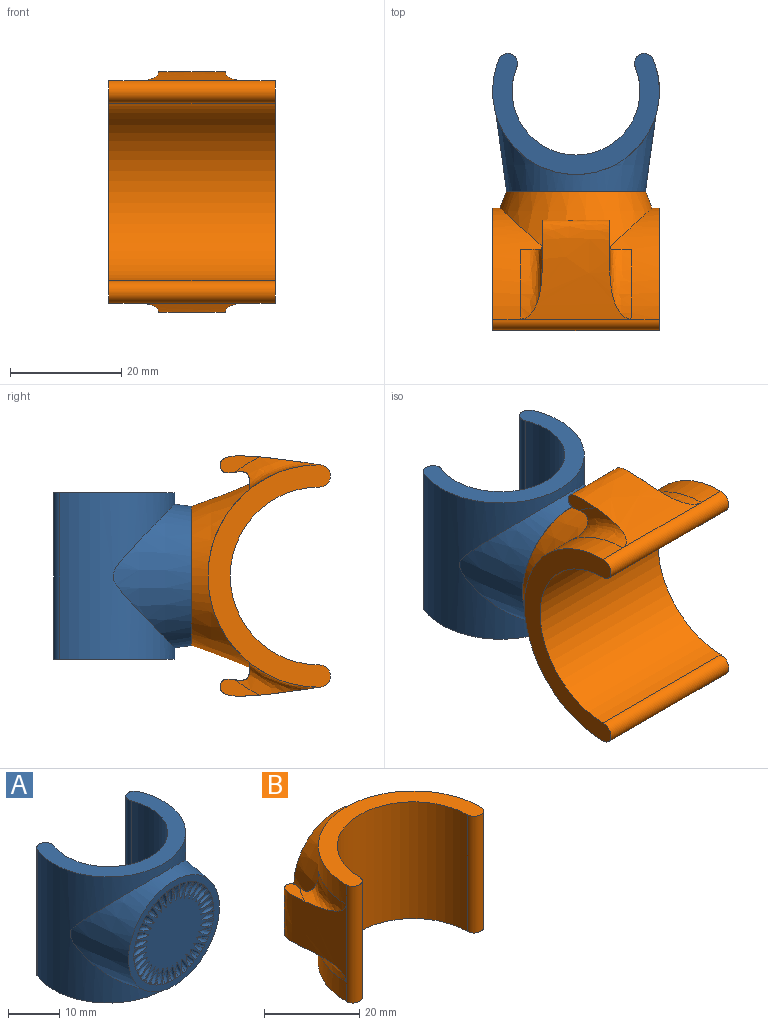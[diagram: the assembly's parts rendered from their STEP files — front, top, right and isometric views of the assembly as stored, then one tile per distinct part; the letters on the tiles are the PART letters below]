
ASSEMBLY  parts=2 mates=1
PART A: 190 faces, bbox 30.1x24.8x30 mm
  f0: cylinder r=15mm len=30mm, axis (0,0,-1), area 1052.1mm2, adj f2,f3,f4,f5,f6,f80,f81,f82
  f1: cylinder r=11.5mm len=30mm, axis (0,0,-1), area 1351.6mm2, adj f2,f3,f4,f5
  f2: cylinder r=1.75mm len=30mm, axis (0,0,-1), area 164.9mm2, adj f0,f1,f4,f5
  f3: cylinder r=1.75mm len=30mm, axis (0,0,-1), area 164.9mm2, adj f0,f1,f4,f5
  f4: plane 30x21.76mm, normal (0,0,1), area 191.3mm2, adj f0,f1,f2,f3
  f5: plane 30x21.76mm, normal (0,0,-1), area 191.3mm2, adj f0,f1,f2,f3
  f6: cone r=12.5mm half-angle=8deg, axis (0,1,0), area 605.5mm2, adj f0,f7
  f7: plane 25.03x25.03mm, normal (0,-1,0), area 357.3mm2, adj f6,f8,f9,f10,f11,f12,f13,f14
  f8: bspline ~3.54x0.78mm, area 2.7mm2, adj f7,f9
  f9: bspline ~3.52x0.92mm, area 2.7mm2, adj f7,f8
  f10: bspline ~3.51x1.07mm, area 2.7mm2, adj f7,f11
  f11: bspline ~3.55x0.84mm, area 2.7mm2, adj f7,f10
  f12: bspline ~3.43x1.64mm, area 2.7mm2, adj f7,f13
  f13: bspline ~3.53x1.2mm, area 2.7mm2, adj f7,f12
  f14: bspline ~3.24x2.17mm, area 2.7mm2, adj f7,f15
  f15: bspline ~3.42x1.75mm, area 2.7mm2, adj f7,f14
  f16: bspline ~2.95x2.62mm, area 2.7mm2, adj f7,f17
  f17: bspline ~3.21x2.26mm, area 2.7mm2, adj f7,f16
  f18: bspline ~3x2.58mm, area 2.7mm2, adj f7,f19
  f19: bspline ~2.9x2.69mm, area 2.7mm2, adj f7,f18
  f20: bspline ~3.28x2.12mm, area 2.7mm2, adj f7,f21
  f21: bspline ~3.04x2.5mm, area 2.7mm2, adj f7,f20
  f22: bspline ~3.46x1.6mm, area 2.7mm2, adj f7,f23
  f23: bspline ~3.3x2.03mm, area 2.7mm2, adj f7,f22
  f24: bspline ~3.54x1.05mm, area 2.7mm2, adj f7,f25
  f25: bspline ~3.46x1.49mm, area 2.7mm2, adj f7,f24
  f26: bspline ~3.54x0.78mm, area 2.7mm2, adj f7,f27
  f27: bspline ~3.52x0.92mm, area 2.7mm2, adj f7,f26
  f28: bspline ~3.51x1.07mm, area 2.7mm2, adj f7,f29
  f29: bspline ~3.55x0.84mm, area 2.7mm2, adj f7,f28
  f30: bspline ~3.43x1.64mm, area 2.7mm2, adj f7,f31
  f31: bspline ~3.53x1.2mm, area 2.7mm2, adj f7,f30
  f32: bspline ~3.24x2.17mm, area 2.7mm2, adj f7,f33
  f33: bspline ~3.42x1.75mm, area 2.7mm2, adj f7,f32
  f34: bspline ~2.95x2.62mm, area 2.7mm2, adj f7,f35
  f35: bspline ~3.21x2.26mm, area 2.7mm2, adj f7,f34
  f36: bspline ~3x2.58mm, area 2.7mm2, adj f7,f37
  f37: bspline ~2.9x2.69mm, area 2.7mm2, adj f7,f36
  f38: bspline ~3.28x2.12mm, area 2.7mm2, adj f7,f39
  f39: bspline ~3.04x2.5mm, area 2.7mm2, adj f7,f38
  f40: bspline ~3.46x1.6mm, area 2.7mm2, adj f7,f41
  f41: bspline ~3.3x2.03mm, area 2.7mm2, adj f7,f40
  f42: bspline ~3.54x1.05mm, area 2.7mm2, adj f7,f43
  f43: bspline ~3.46x1.49mm, area 2.7mm2, adj f7,f42
  f44: bspline ~3.54x0.78mm, area 2.7mm2, adj f7,f45
  f45: bspline ~3.52x0.92mm, area 2.7mm2, adj f7,f44
  f46: bspline ~3.51x1.07mm, area 2.7mm2, adj f7,f47
  f47: bspline ~3.55x0.84mm, area 2.7mm2, adj f7,f46
  f48: bspline ~3.43x1.64mm, area 2.7mm2, adj f7,f49
  f49: bspline ~3.53x1.2mm, area 2.7mm2, adj f7,f48
  f50: bspline ~3.24x2.17mm, area 2.7mm2, adj f7,f51
  f51: bspline ~3.42x1.75mm, area 2.7mm2, adj f7,f50
  f52: bspline ~2.95x2.62mm, area 2.7mm2, adj f7,f53
  f53: bspline ~3.21x2.26mm, area 2.7mm2, adj f7,f52
  f54: bspline ~3x2.58mm, area 2.7mm2, adj f7,f55
  f55: bspline ~2.9x2.69mm, area 2.7mm2, adj f7,f54
  f56: bspline ~3.28x2.12mm, area 2.7mm2, adj f7,f57
  f57: bspline ~3.04x2.5mm, area 2.7mm2, adj f7,f56
  f58: bspline ~3.46x1.6mm, area 2.7mm2, adj f7,f59
  f59: bspline ~3.3x2.03mm, area 2.7mm2, adj f7,f58
  f60: bspline ~3.54x1.05mm, area 2.7mm2, adj f7,f61
  f61: bspline ~3.46x1.49mm, area 2.7mm2, adj f7,f60
  f62: bspline ~3.54x0.78mm, area 2.7mm2, adj f7,f63
  f63: bspline ~3.52x0.92mm, area 2.7mm2, adj f7,f62
  f64: bspline ~3.51x1.07mm, area 2.7mm2, adj f7,f65
  f65: bspline ~3.55x0.84mm, area 2.7mm2, adj f7,f64
  f66: bspline ~3.43x1.64mm, area 2.7mm2, adj f7,f67
  f67: bspline ~3.53x1.2mm, area 2.7mm2, adj f7,f66
  f68: bspline ~3.24x2.17mm, area 2.7mm2, adj f7,f69
  f69: bspline ~3.42x1.75mm, area 2.7mm2, adj f7,f68
  f70: bspline ~2.95x2.62mm, area 2.7mm2, adj f7,f71
  f71: bspline ~3.21x2.26mm, area 2.7mm2, adj f7,f70
  f72: bspline ~3x2.58mm, area 2.7mm2, adj f7,f73
  f73: bspline ~2.9x2.69mm, area 2.7mm2, adj f7,f72
  f74: bspline ~3.28x2.12mm, area 2.7mm2, adj f7,f75
  f75: bspline ~3.04x2.5mm, area 2.7mm2, adj f7,f74
  f76: bspline ~3.46x1.6mm, area 2.7mm2, adj f7,f77
  f77: bspline ~3.3x2.03mm, area 2.7mm2, adj f7,f76
  f78: bspline ~3.54x1.05mm, area 2.7mm2, adj f7,f79
  f79: bspline ~3.46x1.49mm, area 2.7mm2, adj f7,f78
  f80: plane 2.19x1.13mm, normal (-0.03,0.46,-0.89), area 1.7mm2, adj f0,f81,f86,f87
  f81: plane 2.08x1.06mm, normal (0.03,-0.46,-0.89), area 1.6mm2, adj f0,f80,f82,f87
  f82: plane 0.79x0.59mm, normal (-0.07,1,0), area 0.5mm2, adj f0,f81,f83,f87
  f83: plane 1.37x0.73mm, normal (-0.03,0.41,0.91), area 1mm2, adj f0,f82,f84,f87
  f84: plane 1.35x0.82mm, normal (0,0,1), area 1mm2, adj f0,f83,f85,f87
  f85: plane 1.61x0.86mm, normal (0.03,-0.4,0.92), area 1.2mm2, adj f0,f84,f86,f87
  f86: plane 0.78x0.62mm, normal (0.07,-1,0), area 0.5mm2, adj f0,f80,f85,f87
  f87: plane 4.17x1.46mm, normal (1,0.07,0), area 2.7mm2, adj f80,f81,f82,f83,f84,f85,f86
  f88: plane 0.68x0.62mm, normal (0.07,-1,0), area 0.4mm2, adj f0,f89,f95,f96
  f89: plane 1.87x0.88mm, normal (0,0,-1), area 1.3mm2, adj f0,f88,f90,f96
  f90: plane 1.58x0.75mm, normal (0.07,-1,0), area 1.2mm2, adj f0,f89,f91,f96
  f91: plane 0.78x0.52mm, normal (0,0,-1), area 0.4mm2, adj f0,f90,f92,f96
  f92: plane 1.58x0.75mm, normal (-0.07,1,0), area 1.2mm2, adj f0,f91,f93,f96
  f93: plane 1.93x0.77mm, normal (0,0,-1), area 1.3mm2, adj f0,f92,f94,f96
  f94: plane 0.68x0.59mm, normal (-0.07,1,0), area 0.4mm2, adj f0,f93,f95,f96
  f95: plane 4.22x0.93mm, normal (0,0,1), area 3mm2, adj f0,f88,f94,f96
  f96: plane 4.17x2.26mm, normal (1,0.07,0), area 3.6mm2, adj f88,f89,f90,f91,f92,f93,f94,f95
  f97: plane 4.22x0.93mm, normal (0,0,-1), area 3mm2, adj f0,f98,f100,f101
  f98: plane 0.69x0.59mm, normal (-0.07,1,0), area 0.4mm2, adj f0,f97,f99,f101
  f99: plane 4.22x0.93mm, normal (0,0,1), area 3mm2, adj f0,f98,f100,f101
  f100: plane 0.69x0.62mm, normal (0.07,-1,0), area 0.4mm2, adj f0,f97,f99,f101
  f101: plane 4.17x0.69mm, normal (1,0.07,0), area 2.9mm2, adj f97,f98,f99,f100
  f102: extruded ~0.77x0.49mm, area 0.3mm2, adj f0,f103,f134,f135
  f103: extruded ~0.74x0.46mm, area 0.3mm2, adj f0,f102,f104,f135
  f104: extruded ~0.69x0.43mm, area 0.3mm2, adj f0,f103,f105,f135
  f105: extruded ~0.64x0.63mm, area 0.4mm2, adj f0,f104,f106,f135
  f106: extruded ~0.63x0.3mm, area 0.2mm2, adj f0,f105,f107,f135
  f107: extruded ~0.64x0.32mm, area 0.2mm2, adj f0,f106,f108,f135
  f108: extruded ~0.66x0.31mm, area 0.2mm2, adj f0,f107,f109,f135
  f109: extruded ~0.68x0.25mm, area 0.2mm2, adj f0,f108,f110,f135
  f110: plane 0.74x0.47mm, normal (-0.03,0.43,-0.9), area 0.3mm2, adj f0,f109,f111,f135
  f111: extruded ~0.71x0.18mm, area 0.1mm2, adj f0,f110,f112,f135
  f112: extruded ~0.7x0.19mm, area 0.1mm2, adj f0,f111,f113,f135
  f113: extruded ~0.69x0.25mm, area 0.2mm2, adj f0,f112,f114,f135
  f114: extruded ~0.69x0.37mm, area 0.3mm2, adj f0,f113,f115,f135
  f115: extruded ~0.69x0.24mm, area 0.2mm2, adj f0,f114,f116,f135
  f116: extruded ~0.71x0.24mm, area 0.2mm2, adj f0,f115,f117,f135
  f117: extruded ~0.73x0.27mm, area 0.2mm2, adj f0,f116,f118,f135
  f118: extruded ~0.76x0.38mm, area 0.3mm2, adj f0,f117,f119,f135
  f119: extruded ~0.78x0.46mm, area 0.3mm2, adj f0,f118,f120,f135
  f120: extruded ~0.79x0.49mm, area 0.4mm2, adj f0,f119,f121,f135
  f121: extruded ~0.79x0.49mm, area 0.4mm2, adj f0,f120,f122,f135
  f122: extruded ~0.77x0.46mm, area 0.4mm2, adj f0,f121,f123,f135
  f123: extruded ~0.75x0.4mm, area 0.4mm2, adj f0,f122,f124,f135
  f124: extruded ~0.71x0.29mm, area 0.3mm2, adj f0,f123,f125,f135
  f125: plane 0.68x0.67mm, normal (0,0,-1), area 0.4mm2, adj f0,f124,f126,f135
  f126: plane 2.6x0.59mm, normal (-0.07,1,0), area 1.5mm2, adj f0,f125,f127,f135
  f127: plane 0.67x0.6mm, normal (0,0,1), area 0.3mm2, adj f0,f126,f128,f135
  f128: plane 1.78x0.67mm, normal (0.07,-1,0), area 1.2mm2, adj f0,f127,f129,f135
  f129: extruded ~0.71x0.31mm, area 0.3mm2, adj f0,f128,f130,f135
  f130: extruded ~0.74x0.4mm, area 0.4mm2, adj f0,f129,f131,f135
  f131: extruded ~0.77x0.46mm, area 0.4mm2, adj f0,f130,f132,f135
  f132: extruded ~0.79x0.5mm, area 0.4mm2, adj f0,f131,f133,f135
  f133: extruded ~0.79x0.52mm, area 0.4mm2, adj f0,f132,f134,f135
  f134: extruded ~0.78x0.51mm, area 0.4mm2, adj f0,f102,f133,f135
  f135: plane 4.2x2.64mm, normal (1,0.07,0), area 4.9mm2, adj f102,f103,f104,f105,f106,f107,f108,f109
  f136: plane 0.78x0.62mm, normal (0.07,-1,0), area 0.5mm2, adj f0,f137,f142,f143
  f137: plane 1.49x0.85mm, normal (0.03,-0.42,-0.91), area 1.1mm2, adj f0,f136,f138,f143
  f138: plane 1.34x0.83mm, normal (0,0,-1), area 1mm2, adj f0,f137,f139,f143
  f139: plane 1.48x0.74mm, normal (-0.03,0.39,-0.92), area 1.1mm2, adj f0,f138,f140,f143
  f140: plane 0.79x0.59mm, normal (-0.07,1,0), area 0.5mm2, adj f0,f139,f141,f143
  f141: plane 2.08x1.06mm, normal (0.03,-0.46,0.89), area 1.6mm2, adj f0,f140,f142,f143
  f142: plane 2.19x1.13mm, normal (-0.03,0.46,0.89), area 1.7mm2, adj f0,f136,f141,f143
  f143: plane 4.17x1.46mm, normal (1,0.07,0), area 2.7mm2, adj f136,f137,f138,f139,f140,f141,f142
  f144: plane 0.78x0.51mm, normal (0,0.01,-1), area 0.3mm2, adj f0,f145,f188,f189
  f145: plane 0.75x0.57mm, normal (-0.07,1,0), area 0.4mm2, adj f0,f144,f146,f189
  f146: extruded ~0.77x0.52mm, area 0.4mm2, adj f0,f145,f147,f189
  f147: extruded ~0.78x0.57mm, area 0.4mm2, adj f0,f146,f148,f189
  f148: extruded ~0.76x0.59mm, area 0.4mm2, adj f0,f147,f149,f189
  f149: extruded ~0.69x0.59mm, area 0.4mm2, adj f0,f148,f150,f189
  f150: extruded ~0.66x0.42mm, area 0.3mm2, adj f0,f149,f151,f189
  f151: extruded ~0.67x0.24mm, area 0.2mm2, adj f0,f150,f152,f189
  f152: extruded ~0.67x0.13mm, area 0.1mm2, adj f0,f151,f153,f189
  f153: extruded ~0.68x0.11mm, area 0.1mm2, adj f0,f152,f154,f189
  f154: plane 0.68x0.53mm, normal (0.02,-0.3,-0.95), area 0.3mm2, adj f0,f153,f155,f189
  f155: extruded ~0.63x0.38mm, area 0.2mm2, adj f0,f154,f156,f189
  f156: extruded ~0.75x0.6mm, area 0.5mm2, adj f0,f155,f157,f189
  f157: extruded ~0.59x0.19mm, area 0.1mm2, adj f0,f156,f158,f189
  f158: extruded ~0.6x0.27mm, area 0.2mm2, adj f0,f157,f159,f189
  f159: extruded ~0.62x0.3mm, area 0.2mm2, adj f0,f158,f160,f189
  f160: extruded ~0.66x0.28mm, area 0.2mm2, adj f0,f159,f161,f189
  f161: extruded ~0.71x0.39mm, area 0.3mm2, adj f0,f160,f162,f189
  f162: extruded ~0.76x0.54mm, area 0.4mm2, adj f0,f161,f163,f189
  f163: extruded ~0.77x0.46mm, area 0.3mm2, adj f0,f162,f164,f189
  f164: extruded ~0.77x0.35mm, area 0.3mm2, adj f0,f163,f165,f189
  f165: extruded ~0.77x0.26mm, area 0.2mm2, adj f0,f164,f166,f189
  f166: extruded ~0.76x0.27mm, area 0.2mm2, adj f0,f165,f167,f189
  f167: extruded ~0.76x0.22mm, area 0.2mm2, adj f0,f166,f168,f189
  f168: extruded ~0.77x0.23mm, area 0.2mm2, adj f0,f167,f169,f189
  f169: extruded ~0.77x0.3mm, area 0.2mm2, adj f0,f168,f170,f189
  f170: extruded ~0.77x0.37mm, area 0.2mm2, adj f0,f169,f171,f189
  f171: extruded ~0.77x0.57mm, area 0.4mm2, adj f0,f170,f172,f189
  f172: extruded ~0.72x0.41mm, area 0.3mm2, adj f0,f171,f173,f189
  f173: extruded ~0.67x0.42mm, area 0.3mm2, adj f0,f172,f174,f189
  f174: extruded ~0.63x0.51mm, area 0.3mm2, adj f0,f173,f175,f189
  f175: extruded ~0.63x0.58mm, area 0.4mm2, adj f0,f174,f176,f189
  f176: extruded ~0.64x0.34mm, area 0.2mm2, adj f0,f175,f177,f189
  f177: plane 0.73x0.55mm, normal (-0.02,0.36,-0.93), area 0.4mm2, adj f0,f176,f178,f189
  f178: extruded ~0.7x0.24mm, area 0.2mm2, adj f0,f177,f179,f189
  f179: extruded ~0.69x0.42mm, area 0.3mm2, adj f0,f178,f180,f189
  f180: extruded ~0.69x0.41mm, area 0.3mm2, adj f0,f179,f181,f189
  f181: extruded ~0.71x0.22mm, area 0.2mm2, adj f0,f180,f182,f189
  f182: extruded ~0.73x0.26mm, area 0.2mm2, adj f0,f181,f183,f189
  f183: extruded ~0.75x0.27mm, area 0.2mm2, adj f0,f182,f184,f189
  f184: extruded ~0.78x0.44mm, area 0.3mm2, adj f0,f183,f185,f189
  f185: extruded ~0.77x0.24mm, area 0.2mm2, adj f0,f184,f186,f189
  f186: extruded ~0.76x0.24mm, area 0.2mm2, adj f0,f185,f187,f189
  f187: extruded ~0.75x0.25mm, area 0.2mm2, adj f0,f186,f188,f189
  f188: plane 0.75x0.39mm, normal (0.07,-1,0), area 0.3mm2, adj f0,f144,f187,f189
  f189: plane 4.22x2.47mm, normal (1,0.07,0), area 4.3mm2, adj f144,f145,f146,f147,f148,f149,f150,f151
PART B: 91 faces, bbox 48x25.6x33 mm
  f0: bspline ~3.54x0.78mm, area 2.7mm2, adj f1,f2
  f1: bspline ~3.52x0.92mm, area 2.7mm2, adj f0,f2
  f2: plane 25.03x25.03mm, normal (0,1,0), area 357.3mm2, adj f0,f1,f3,f4,f5,f6,f7,f8
  f3: bspline ~3.51x1.07mm, area 2.7mm2, adj f2,f4
  f4: bspline ~3.55x0.84mm, area 2.7mm2, adj f2,f3
  f5: bspline ~3.43x1.64mm, area 2.7mm2, adj f2,f6
  f6: bspline ~3.53x1.2mm, area 2.7mm2, adj f2,f5
  f7: bspline ~3.24x2.17mm, area 2.7mm2, adj f2,f8
  f8: bspline ~3.42x1.75mm, area 2.7mm2, adj f2,f7
  f9: bspline ~2.95x2.62mm, area 2.7mm2, adj f2,f10
  f10: bspline ~3.21x2.26mm, area 2.7mm2, adj f2,f9
  f11: bspline ~3x2.58mm, area 2.7mm2, adj f2,f12
  f12: bspline ~2.9x2.69mm, area 2.7mm2, adj f2,f11
  f13: bspline ~3.28x2.12mm, area 2.7mm2, adj f2,f14
  f14: bspline ~3.04x2.5mm, area 2.7mm2, adj f2,f13
  f15: bspline ~3.46x1.6mm, area 2.7mm2, adj f2,f16
  f16: bspline ~3.3x2.03mm, area 2.7mm2, adj f2,f15
  f17: bspline ~3.54x1.05mm, area 2.7mm2, adj f2,f18
  f18: bspline ~3.46x1.49mm, area 2.7mm2, adj f2,f17
  f19: bspline ~3.54x0.78mm, area 2.7mm2, adj f2,f20
  f20: bspline ~3.52x0.92mm, area 2.7mm2, adj f2,f19
  f21: bspline ~3.51x1.07mm, area 2.7mm2, adj f2,f22
  f22: bspline ~3.55x0.84mm, area 2.7mm2, adj f2,f21
  f23: bspline ~3.43x1.64mm, area 2.7mm2, adj f2,f24
  f24: bspline ~3.53x1.2mm, area 2.7mm2, adj f2,f23
  f25: bspline ~3.24x2.17mm, area 2.7mm2, adj f2,f26
  f26: bspline ~3.42x1.75mm, area 2.7mm2, adj f2,f25
  f27: bspline ~2.95x2.62mm, area 2.7mm2, adj f2,f28
  f28: bspline ~3.21x2.26mm, area 2.7mm2, adj f2,f27
  f29: bspline ~3x2.58mm, area 2.7mm2, adj f2,f30
  f30: bspline ~2.9x2.69mm, area 2.7mm2, adj f2,f29
  f31: bspline ~3.28x2.12mm, area 2.7mm2, adj f2,f32
  f32: bspline ~3.04x2.5mm, area 2.7mm2, adj f2,f31
  f33: bspline ~3.46x1.6mm, area 2.7mm2, adj f2,f34
  f34: bspline ~3.3x2.03mm, area 2.7mm2, adj f2,f33
  f35: bspline ~3.54x1.05mm, area 2.7mm2, adj f2,f36
  f36: bspline ~3.46x1.49mm, area 2.7mm2, adj f2,f35
  f37: bspline ~3.54x0.78mm, area 2.7mm2, adj f2,f38
  f38: bspline ~3.52x0.92mm, area 2.7mm2, adj f2,f37
  f39: bspline ~3.51x1.07mm, area 2.7mm2, adj f2,f40
  f40: bspline ~3.55x0.84mm, area 2.7mm2, adj f2,f39
  f41: bspline ~3.43x1.64mm, area 2.7mm2, adj f2,f42
  f42: bspline ~3.53x1.2mm, area 2.7mm2, adj f2,f41
  f43: bspline ~3.24x2.17mm, area 2.7mm2, adj f2,f44
  f44: bspline ~3.42x1.75mm, area 2.7mm2, adj f2,f43
  f45: bspline ~2.95x2.62mm, area 2.7mm2, adj f2,f46
  f46: bspline ~3.21x2.26mm, area 2.7mm2, adj f2,f45
  f47: bspline ~3x2.58mm, area 2.7mm2, adj f2,f48
  f48: bspline ~2.9x2.69mm, area 2.7mm2, adj f2,f47
  f49: bspline ~3.28x2.12mm, area 2.7mm2, adj f2,f50
  f50: bspline ~3.04x2.5mm, area 2.7mm2, adj f2,f49
  f51: bspline ~3.46x1.6mm, area 2.7mm2, adj f2,f52
  f52: bspline ~3.3x2.03mm, area 2.7mm2, adj f2,f51
  f53: bspline ~3.54x1.05mm, area 2.7mm2, adj f2,f54
  f54: bspline ~3.46x1.49mm, area 2.7mm2, adj f2,f53
  f55: bspline ~3.54x0.78mm, area 2.7mm2, adj f2,f56
  f56: bspline ~3.52x0.92mm, area 2.7mm2, adj f2,f55
  f57: bspline ~3.51x1.07mm, area 2.7mm2, adj f2,f58
  f58: bspline ~3.55x0.84mm, area 2.7mm2, adj f2,f57
  f59: bspline ~3.43x1.64mm, area 2.7mm2, adj f2,f60
  f60: bspline ~3.53x1.2mm, area 2.7mm2, adj f2,f59
  f61: bspline ~3.24x2.17mm, area 2.7mm2, adj f2,f62
  f62: bspline ~3.42x1.75mm, area 2.7mm2, adj f2,f61
  f63: bspline ~2.95x2.62mm, area 2.7mm2, adj f2,f64
  f64: bspline ~3.21x2.26mm, area 2.7mm2, adj f2,f63
  f65: bspline ~3x2.58mm, area 2.7mm2, adj f2,f66
  f66: bspline ~2.9x2.69mm, area 2.7mm2, adj f2,f65
  f67: bspline ~3.28x2.12mm, area 2.7mm2, adj f2,f68
  f68: bspline ~3.04x2.5mm, area 2.7mm2, adj f2,f67
  f69: bspline ~3.46x1.6mm, area 2.7mm2, adj f2,f70
  f70: bspline ~3.3x2.03mm, area 2.7mm2, adj f2,f69
  f71: bspline ~3.54x1.05mm, area 2.7mm2, adj f2,f72
  f72: bspline ~3.46x1.49mm, area 2.7mm2, adj f2,f71
  f73: cylinder r=20mm len=40mm, axis (0,0,-1), area 282.6mm2, adj f74,f75,f78,f79,f80,f87,f89,f90
  f74: extruded ~20x17.8mm, area 368.7mm2, adj f73,f76,f79,f82,f83,f88,f89,f90
  f75: extruded ~20x17.8mm, area 368.7mm2, adj f73,f76,f78,f84,f85,f86,f87,f90
  f76: cylinder r=20mm len=40mm, axis (0,0,-1), area 329.1mm2, adj f74,f75,f78,f79,f81,f86,f88,f90
  f77: cylinder r=16mm len=32mm, axis (0,0,-1), area 1508mm2, adj f78,f79,f80,f81
  f78: cylinder r=2mm len=30mm, axis (0,0,-1), area 188.5mm2, adj f73,f75,f76,f77,f80,f81
  f79: cylinder r=2mm len=30mm, axis (0,0,-1), area 188.5mm2, adj f73,f74,f76,f77,f80,f81
  f80: plane 40x22mm, normal (0,0,1), area 238.8mm2, adj f73,f77,f78,f79
  f81: plane 40x22mm, normal (0,0,-1), area 238.8mm2, adj f76,f77,f78,f79
  f82: plane 7.69x3.77mm, normal (0,0,1), area 13.1mm2, adj f74,f89
  f83: plane 7.69x3.77mm, normal (0,0,-1), area 13.1mm2, adj f74,f88
  f84: plane 7.69x3.77mm, normal (0,0,1), area 13.1mm2, adj f75,f87
  f85: plane 7.69x3.77mm, normal (0,0,-1), area 13.1mm2, adj f75,f86
  f86: bspline ~16.52x8.88mm, area 62.7mm2, adj f75,f76,f85
  f87: bspline ~16.52x8.88mm, area 62.7mm2, adj f73,f75,f84
  f88: bspline ~16.52x8.88mm, area 62.7mm2, adj f74,f76,f83
  f89: bspline ~16.52x8.88mm, area 62.7mm2, adj f73,f74,f82
  f90: cone r=12.5mm half-angle=21deg, axis (0,-1,0), area 613.6mm2, adj f2,f73,f74,f75,f76
PLACE A t=(0.02,1.99,-0.33)mm
PLACE B rot(axis=(0,1,0),90deg) t=(0.02,1.99,-0.33)mm
MATE planar B.f90 <-> A.f6  axis (0,1,0) through (0.02,-16.01,-0.33)mm
